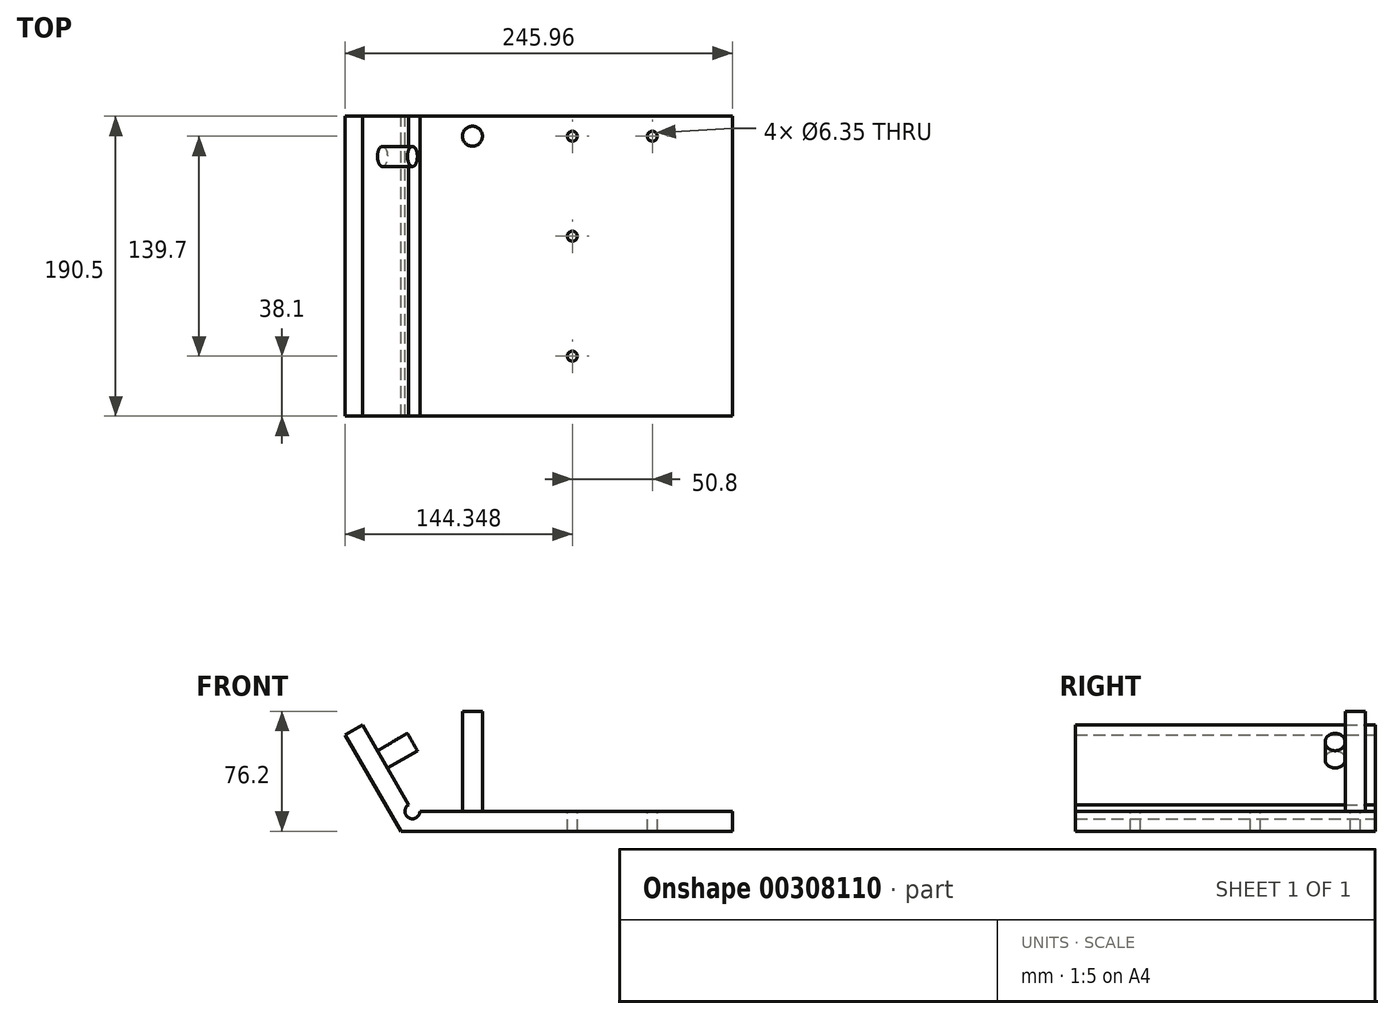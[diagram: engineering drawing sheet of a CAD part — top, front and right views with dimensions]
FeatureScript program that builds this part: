
annotation { "Feature Type Name" : "Feature", "Feature Type Description" : "" }
export const myFeature = defineFeature(function(context is Context, id is Id, definition is map)
    precondition{}
    {
        {
            var Q0;
            Q0=qCreatedBy(makeId("Front.planeOp"),FACE);
            var sketch = newSketch(context, id + "F0", { "sketchPlane" : qUnion([Q0])});
            skLineSegment(sketch, "E0.bottom", {"start": v(12.1, 0) * mm, "end": v(210.54, 0) * mm});
            skLineSegment(sketch, "E0.top", {"start": v(0, -12.7) * mm, "end": v(210.54, -12.7) * mm});
            skLineSegment(sketch, "E0.right", {"start": v(210.54, 0) * mm, "end": v(210.54, -12.7) * mm});
            skArc(sketch, "E1", {"start": v(4.96, 4.12) * mm, "mid": v(4.96, -4.12) * mm, "end": v(12.1, 0) * mm});
            skLineSegment(sketch, "E2", {"start": v(0, -12.7) * mm, "end": v(-35.42, 48.65) * mm});
            skLineSegment(sketch, "E3", {"start": v(4.96, 4.12) * mm, "end": v(-24.4, 55) * mm});
            skLineSegment(sketch, "E4", {"start": v(-35.42, 48.65) * mm, "end": v(-24.4, 55) * mm});
            skSolve(sketch);
        }
        {
            var Q0;
            Q0 = qSketchRegion(id + "F0", true);
            extrude(context, id + "F1", {"entities" : qUnion([Q0]), "depth" : 190.5 * mm});
        }
        {
            var Q0;
            Q0=makeQuery(id+"F1.opExtrude","SWEPT_FACE",FACE,{"disambiguationData":[OSD([sQuery(id+"F0.wireOp",EDGE,"E3")])]});
            var sketch = newSketch(context, id + "F2", { "sketchPlane" : qUnion([Q0])});
            skCircle(sketch, "E5", {"center": v(-25.55, 34.43) * mm, "radius": 6.35 * mm});
            skLineSegment(sketch, "E6", {"start": v(0, 59.83) * mm, "end": v(0, 34.43) * mm});
            skLineSegment(sketch, "E7", {"start": v(0, 34.43) * mm, "end": v(-25.55, 34.43) * mm});
            skSolve(sketch);
        }
        {
            var Q0;
            Q0 = qSketchRegion(id + "F2", true);
            extrude(context, id + "F3", {"entities" : qUnion([Q0]), "operationType" : NewBodyOperationType.ADD, "depth" : 22 * mm});
        }
        {
            var Q0;
            Q0=makeQuery(id+"F1.opExtrude","CAP_FACE",FACE,{"disambiguationData":[OSD([sQuery(id+"F0.wireOp",EDGE,"E0.bottom"),sQuery(id+"F0.wireOp",EDGE,"E0.top"),sQuery(id+"F0.wireOp",EDGE,"E0.right"),sQuery(id+"F0.wireOp",EDGE,"E1"),sQuery(id+"F0.wireOp",EDGE,"E2"),sQuery(id+"F0.wireOp",EDGE,"E3"),sQuery(id+"F0.wireOp",EDGE,"E4")])],"isStart":true});
            var sketch = newSketch(context, id + "F4", { "sketchPlane" : qUnion([Q0])});
            skLineSegment(sketch, "E8", {"start": v(-45.44, -12.7) * mm, "end": v(-45.44, 0) * mm});
            skLineSegment(sketch, "E9", {"start": v(-12.1, 0) * mm, "end": v(-12.1, -12.7) * mm});
            skLineSegment(sketch, "E10", {"start": v(-12.1, 0) * mm, "end": v(-45.44, 0) * mm});
            skLineSegment(sketch, "E11", {"start": v(0, -12.7) * mm, "end": v(-45.44, -12.7) * mm});
            skLineSegment(sketch, "E12", {"start": v(0, -12.7) * mm, "end": v(-108.94, -12.7) * mm});
            skSolve(sketch);
        }
        {
            var Q0;
            Q0=makeQuery(id+"F1.opExtrude","SWEPT_FACE",FACE,{"disambiguationData":[OSD([sQuery(id+"F0.wireOp",EDGE,"E0.bottom")])]});
            var sketch = newSketch(context, id + "F5", { "sketchPlane" : qUnion([Q0])});
            skCircle(sketch, "E13", {"center": v(108.93, -152.4) * mm, "radius": 3.18 * mm});
            skLineSegment(sketch, "E14", {"start": v(12.1, -190.5) * mm, "end": v(12.1, -76.2) * mm});
            skLineSegment(sketch, "E15", {"start": v(108.93, -152.4) * mm, "end": v(108.93, -76.2) * mm});
            skCircle(sketch, "E16", {"center": v(108.93, -76.2) * mm, "radius": 3.18 * mm});
            skCircle(sketch, "E17", {"center": v(159.73, -12.7) * mm, "radius": 3.18 * mm});
            skCircle(sketch, "E18", {"center": v(108.93, -12.7) * mm, "radius": 3.18 * mm});
            skSolve(sketch);
        }
        {
            var Q0;
            Q0=sQuery(id+"F5.wireOp",VERTEX,"E18.center");
            var Q1;
            Q1=sQuery(id+"F5.wireOp",VERTEX,"E17.center");
            var Q2;
            Q2=sQuery(id+"F5.wireOp",VERTEX,"E16.center");
            var Q3;
            Q3=sQuery(id+"F5.wireOp",VERTEX,"E13.center");
            var Q4;
            Q4=makeQuery(id+"F1.opExtrude","SWEPT_BODY",BODY,{"disambiguationData":[OSD([sQuery(id+"F0.wireOp",EDGE,"E0.bottom"),sQuery(id+"F0.wireOp",EDGE,"E0.top"),sQuery(id+"F0.wireOp",EDGE,"E0.right"),sQuery(id+"F0.wireOp",EDGE,"E1"),sQuery(id+"F0.wireOp",EDGE,"E2"),sQuery(id+"F0.wireOp",EDGE,"E3"),sQuery(id+"F0.wireOp",EDGE,"E4")])]});
            hole(context, id + "F6", {"style" : HoleStyle.SIMPLE, "endStyle" : HoleEndStyle.THROUGH, "holeDiameter" : 6.35 * mm, "tappedDepth" : 12.7 * mm, "tapClearance" : 3, "locations" : qUnion([Q0, Q1, Q2, Q3]), "scope" : qUnion([Q4])});
        }
        {
            var Q0;
            Q0=makeQuery(id+"F1.opExtrude","SWEPT_FACE",FACE,{"disambiguationData":[OSD([sQuery(id+"F0.wireOp",EDGE,"E0.bottom")])]});
            var sketch = newSketch(context, id + "F7", { "sketchPlane" : qUnion([Q0])});
            skCircle(sketch, "E19", {"center": v(45.45, -12.7) * mm, "radius": 6.35 * mm});
            skSolve(sketch);
        }
        {
            var Q0;
            Q0 = qSketchRegion(id + "F7", true);
            extrude(context, id + "F8", {"entities" : qUnion([Q0]), "operationType" : NewBodyOperationType.ADD, "depth" : 63.5 * mm});
        }
    });
